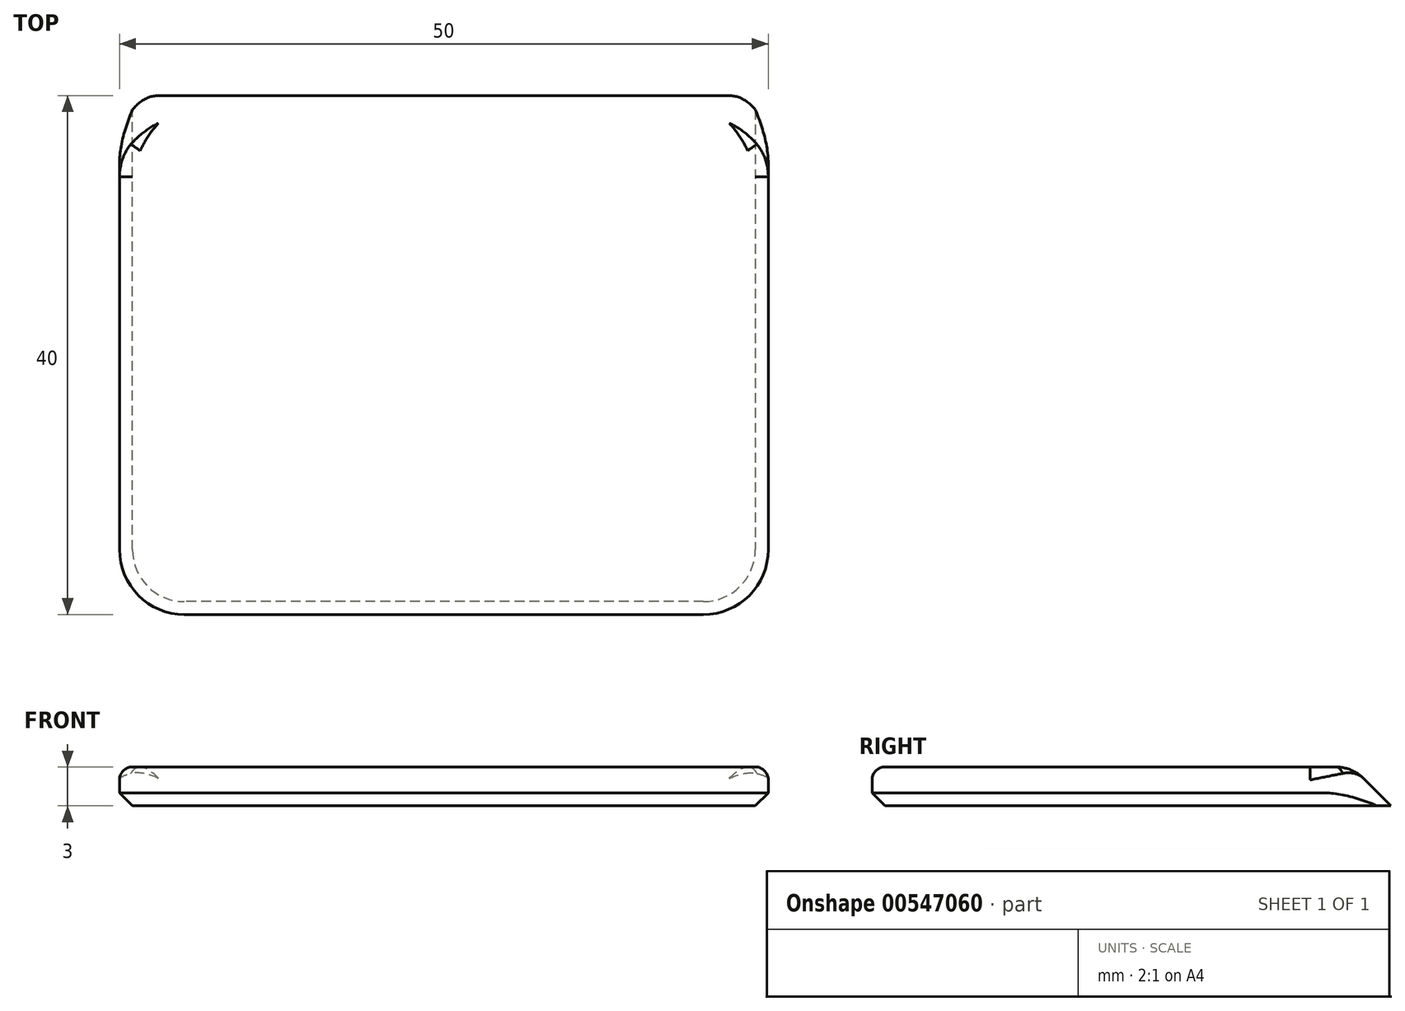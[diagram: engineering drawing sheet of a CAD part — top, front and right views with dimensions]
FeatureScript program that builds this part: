
annotation { "Feature Type Name" : "Feature", "Feature Type Description" : "" }
export const myFeature = defineFeature(function(context is Context, id is Id, definition is map)
    precondition{}
    {
        {
            var Q0;
            Q0=qCreatedBy(makeId("Top.planeOp"),FACE);
            var sketch = newSketch(context, id + "F0", { "sketchPlane" : qUnion([Q0])});
            skLineSegment(sketch, "E0.bottom", {"start": v(25, 20) * mm, "end": v(-25, 20) * mm});
            skLineSegment(sketch, "E0.top", {"start": v(20, -20) * mm, "end": v(-20, -20) * mm});
            skLineSegment(sketch, "E0.left", {"start": v(25, 20) * mm, "end": v(25, -15) * mm});
            skLineSegment(sketch, "E0.right", {"start": v(-25, 20) * mm, "end": v(-25, -15) * mm});
            skPoint(sketch, "E0.middle", {"position": v(0, 0) * mm});
            skPoint(sketch, "E1.visualSharp", {"position": v(-25, -20) * mm});
            skArc(sketch, "E1.filletArc", {"start": v(-25, -15) * mm, "mid": v(-23.54, -18.54) * mm, "end": v(-20, -20) * mm});
            skPoint(sketch, "E2.visualSharp", {"position": v(25, -20) * mm});
            skArc(sketch, "E2.filletArc", {"start": v(20, -20) * mm, "mid": v(23.54, -18.54) * mm, "end": v(25, -15) * mm});
            skSolve(sketch);
        }
        {
            var Q0;
            Q0 = qSketchRegion(id + "F0", true);
            extrude(context, id + "F1", {"entities" : qUnion([Q0]), "depth" : 3 * mm, "offsetDistance" : 25 * mm});
        }
        {
            var Q0;
            Q0=makeQuery(id+"F1.opExtrude","CAP_EDGE",EDGE,{"disambiguationData":[OSD([sQuery(id+"F0.wireOp",EDGE,"E0.bottom")])],"isStart":false});
            chamfer(context, id + "F2", {"entities" : qUnion([Q0]), "width" : 3 * mm, "tangentPropagation" : true});
        }
        {
            var Q0;
            Q0=makeQuery(id+"F2.opChamfer","BLEND_EDGE",EDGE,{"blendedFrom":[makeQuery(id+"F1.opExtrude","CAP_EDGE",EDGE,{"disambiguationData":[OSD([sQuery(id+"F0.wireOp",EDGE,"E0.bottom")])],"isStart":false}),makeQuery(id+"F1.opExtrude","SWEPT_FACE",FACE,{"disambiguationData":[OSD([sQuery(id+"F0.wireOp",EDGE,"E0.right")])]})],"blendedInto":[makeQuery(id+"F1.opExtrude","SWEPT_FACE",FACE,{"disambiguationData":[OSD([sQuery(id+"F0.wireOp",EDGE,"E0.right")])]})]});
            var Q1;
            Q1=makeQuery(id+"F2.opChamfer","BLEND_EDGE",EDGE,{"blendedFrom":[makeQuery(id+"F1.opExtrude","CAP_EDGE",EDGE,{"disambiguationData":[OSD([sQuery(id+"F0.wireOp",EDGE,"E0.bottom")])],"isStart":false}),makeQuery(id+"F1.opExtrude","SWEPT_FACE",FACE,{"disambiguationData":[OSD([sQuery(id+"F0.wireOp",EDGE,"E0.left")])]})],"blendedInto":[makeQuery(id+"F1.opExtrude","SWEPT_FACE",FACE,{"disambiguationData":[OSD([sQuery(id+"F0.wireOp",EDGE,"E0.left")])]})]});
            var Q2;
            {var subQ0=sQuery(id+"F0.wireOp",EDGE,"E0.bottom");Q2=makeQuery(id+"F2.opChamfer","BLEND_EDGE",EDGE,{"blendedFrom":[makeQuery(id+"F1.opExtrude","CAP_EDGE",EDGE,{"disambiguationData":[OSD([subQ0])],"isStart":false}),makeQuery(id+"F1.opExtrude","CAP_FACE",FACE,{"disambiguationData":[OSD([subQ0,sQuery(id+"F0.wireOp",EDGE,"E0.top"),sQuery(id+"F0.wireOp",EDGE,"E0.left"),sQuery(id+"F0.wireOp",EDGE,"E0.right"),sQuery(id+"F0.wireOp",EDGE,"E1.filletArc"),sQuery(id+"F0.wireOp",EDGE,"E2.filletArc")])],"isStart":false})],"blendedInto":[makeQuery(id+"F1.opExtrude","CAP_FACE",FACE,{"disambiguationData":[OSD([subQ0,sQuery(id+"F0.wireOp",EDGE,"E0.top"),sQuery(id+"F0.wireOp",EDGE,"E0.left"),sQuery(id+"F0.wireOp",EDGE,"E0.right"),sQuery(id+"F0.wireOp",EDGE,"E1.filletArc"),sQuery(id+"F0.wireOp",EDGE,"E2.filletArc")])],"isStart":false})]});}
            fillet(context, id + "F3", {"entities" : qUnion([Q0, Q1, Q2]), "radius" : 3 * mm, "tangentPropagation" : true, "allowEdgeOverflow" : false});
        }
        {
            var Q0;
            Q0=makeQuery(id+"F1.opExtrude","CAP_EDGE",EDGE,{"disambiguationData":[OSD([sQuery(id+"F0.wireOp",EDGE,"E0.right")])],"isStart":false});
            var Q1;
            Q1=makeQuery(id+"F1.opExtrude","CAP_EDGE",EDGE,{"disambiguationData":[OSD([sQuery(id+"F0.wireOp",EDGE,"E1.filletArc")])],"isStart":false});
            var Q2;
            Q2=makeQuery(id+"F1.opExtrude","CAP_EDGE",EDGE,{"disambiguationData":[OSD([sQuery(id+"F0.wireOp",EDGE,"E0.top")])],"isStart":false});
            var Q3;
            Q3=makeQuery(id+"F1.opExtrude","CAP_EDGE",EDGE,{"disambiguationData":[OSD([sQuery(id+"F0.wireOp",EDGE,"E2.filletArc")])],"isStart":false});
            var Q4;
            Q4=makeQuery(id+"F1.opExtrude","CAP_EDGE",EDGE,{"disambiguationData":[OSD([sQuery(id+"F0.wireOp",EDGE,"E0.left")])],"isStart":false});
            var Q5;
            {var subQ0=sQuery(id+"F0.wireOp",EDGE,"E0.right");var subQ1=sQuery(id+"F0.wireOp",EDGE,"E0.bottom");Q5=makeQuery(id+"F3.opFillet","BLEND_EDGE",EDGE,{"blendedFrom":[makeQuery(id+"F2.opChamfer","BLEND_EDGE",EDGE,{"blendedFrom":[makeQuery(id+"F1.opExtrude","CAP_EDGE",EDGE,{"disambiguationData":[OSD([subQ1])],"isStart":false}),makeQuery(id+"F1.opExtrude","SWEPT_FACE",FACE,{"disambiguationData":[OSD([subQ0])]})],"blendedInto":[makeQuery(id+"F1.opExtrude","SWEPT_FACE",FACE,{"disambiguationData":[OSD([subQ0])]})]}),makeQuery(id+"F1.opExtrude","CAP_FACE",FACE,{"disambiguationData":[OSD([subQ1,sQuery(id+"F0.wireOp",EDGE,"E0.top"),sQuery(id+"F0.wireOp",EDGE,"E0.left"),subQ0,sQuery(id+"F0.wireOp",EDGE,"E1.filletArc"),sQuery(id+"F0.wireOp",EDGE,"E2.filletArc")])],"isStart":false})],"blendedInto":[makeQuery(id+"F1.opExtrude","CAP_FACE",FACE,{"disambiguationData":[OSD([subQ1,sQuery(id+"F0.wireOp",EDGE,"E0.top"),sQuery(id+"F0.wireOp",EDGE,"E0.left"),subQ0,sQuery(id+"F0.wireOp",EDGE,"E1.filletArc"),sQuery(id+"F0.wireOp",EDGE,"E2.filletArc")])],"isStart":false})]});}
            var Q6;
            {var subQ0=sQuery(id+"F0.wireOp",EDGE,"E0.right");var subQ1=sQuery(id+"F0.wireOp",EDGE,"E0.bottom");var subQ2=makeQuery(id+"F1.opExtrude","CAP_EDGE",EDGE,{"disambiguationData":[OSD([subQ1])],"isStart":false});Q6=makeQuery(id+"F3.opFillet","BLEND_EDGE",EDGE,{"blendedFrom":[makeQuery(id+"F2.opChamfer","BLEND_EDGE",EDGE,{"blendedFrom":[subQ2,makeQuery(id+"F1.opExtrude","CAP_FACE",FACE,{"disambiguationData":[OSD([subQ1,sQuery(id+"F0.wireOp",EDGE,"E0.top"),sQuery(id+"F0.wireOp",EDGE,"E0.left"),subQ0,sQuery(id+"F0.wireOp",EDGE,"E1.filletArc"),sQuery(id+"F0.wireOp",EDGE,"E2.filletArc")])],"isStart":false})],"blendedInto":[makeQuery(id+"F1.opExtrude","CAP_FACE",FACE,{"disambiguationData":[OSD([subQ1,sQuery(id+"F0.wireOp",EDGE,"E0.top"),sQuery(id+"F0.wireOp",EDGE,"E0.left"),subQ0,sQuery(id+"F0.wireOp",EDGE,"E1.filletArc"),sQuery(id+"F0.wireOp",EDGE,"E2.filletArc")])],"isStart":false})]}),makeQuery(id+"F2.opChamfer","BLEND_EDGE",EDGE,{"blendedFrom":[subQ2,makeQuery(id+"F1.opExtrude","SWEPT_FACE",FACE,{"disambiguationData":[OSD([subQ0])]})],"blendedInto":[makeQuery(id+"F1.opExtrude","SWEPT_FACE",FACE,{"disambiguationData":[OSD([subQ0])]})]})],"blendedInto":[]});}
            var Q7;
            {var subQ0=sQuery(id+"F0.wireOp",EDGE,"E0.left");var subQ1=sQuery(id+"F0.wireOp",EDGE,"E0.bottom");var subQ2=makeQuery(id+"F1.opExtrude","CAP_EDGE",EDGE,{"disambiguationData":[OSD([subQ1])],"isStart":false});Q7=makeQuery(id+"F3.opFillet","BLEND_EDGE",EDGE,{"blendedFrom":[makeQuery(id+"F2.opChamfer","BLEND_EDGE",EDGE,{"blendedFrom":[subQ2,makeQuery(id+"F1.opExtrude","CAP_FACE",FACE,{"disambiguationData":[OSD([subQ1,sQuery(id+"F0.wireOp",EDGE,"E0.top"),subQ0,sQuery(id+"F0.wireOp",EDGE,"E0.right"),sQuery(id+"F0.wireOp",EDGE,"E1.filletArc"),sQuery(id+"F0.wireOp",EDGE,"E2.filletArc")])],"isStart":false})],"blendedInto":[makeQuery(id+"F1.opExtrude","CAP_FACE",FACE,{"disambiguationData":[OSD([subQ1,sQuery(id+"F0.wireOp",EDGE,"E0.top"),subQ0,sQuery(id+"F0.wireOp",EDGE,"E0.right"),sQuery(id+"F0.wireOp",EDGE,"E1.filletArc"),sQuery(id+"F0.wireOp",EDGE,"E2.filletArc")])],"isStart":false})]}),makeQuery(id+"F2.opChamfer","BLEND_EDGE",EDGE,{"blendedFrom":[subQ2,makeQuery(id+"F1.opExtrude","SWEPT_FACE",FACE,{"disambiguationData":[OSD([subQ0])]})],"blendedInto":[makeQuery(id+"F1.opExtrude","SWEPT_FACE",FACE,{"disambiguationData":[OSD([subQ0])]})]})],"blendedInto":[]});}
            fillet(context, id + "F4", {"entities" : qUnion([Q0, Q1, Q2, Q3, Q4, Q5, Q6, Q7]), "radius" : 1 * mm, "tangentPropagation" : true, "allowEdgeOverflow" : false});
        }
        {
            var Q0;
            Q0=makeQuery(id+"F1.opExtrude","CAP_EDGE",EDGE,{"disambiguationData":[OSD([sQuery(id+"F0.wireOp",EDGE,"E0.top")])],"isStart":true});
            var Q1;
            Q1=makeQuery(id+"F1.opExtrude","CAP_EDGE",EDGE,{"disambiguationData":[OSD([sQuery(id+"F0.wireOp",EDGE,"E1.filletArc")])],"isStart":true});
            var Q2;
            Q2=makeQuery(id+"F1.opExtrude","CAP_EDGE",EDGE,{"disambiguationData":[OSD([sQuery(id+"F0.wireOp",EDGE,"E0.right")])],"isStart":true});
            var Q3;
            Q3=makeQuery(id+"F1.opExtrude","CAP_EDGE",EDGE,{"disambiguationData":[OSD([sQuery(id+"F0.wireOp",EDGE,"E0.left")])],"isStart":true});
            var Q4;
            Q4=makeQuery(id+"F1.opExtrude","CAP_EDGE",EDGE,{"disambiguationData":[OSD([sQuery(id+"F0.wireOp",EDGE,"E2.filletArc")])],"isStart":true});
            chamfer(context, id + "F5", {"entities" : qUnion([Q0, Q1, Q2, Q3, Q4]), "width" : 1 * mm});
        }
    });
